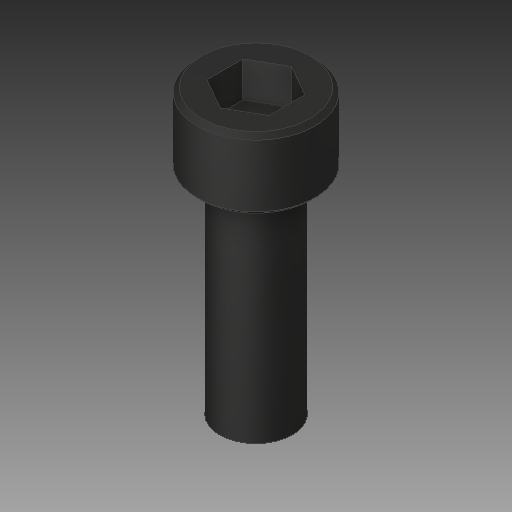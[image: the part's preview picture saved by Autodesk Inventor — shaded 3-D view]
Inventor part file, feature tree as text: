
AUTODESK INVENTOR PART (.ipt)
format: ipt  version: 2018 (Build 220112000, 112)  size: 104,960 bytes
history: native  units: in
note: dims shown in document units (in); Inventor stores cm internally (conversion verified against a paired STEP export)
features: chamfer x1
ambient origin geometry x8: Origin, YZ Plane, XZ Plane, XY Plane, X Axis, Y Axis, Z Axis, Center Point
bodies: Solid1 (feature_tree)
feature tree (1):
  chamfer  "Chamfer2"  [1 undecoded]
note: 1 required parameter value undecoded (feature->parameter linkage not recoverable at this tier; creation-order binding heuristic only, values carry confidence <= 0.55)
